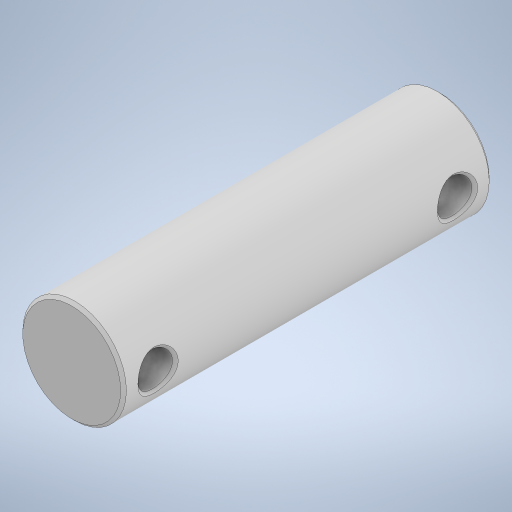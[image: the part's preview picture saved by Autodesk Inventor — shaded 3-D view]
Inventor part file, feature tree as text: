
AUTODESK INVENTOR PART (.ipt)
format: ipt  version: 2023 (Build 270158000, 158)  size: 261,632 bytes
history: native  units: mm
features: sketch x2, extrude x1, hole x1, chamfer x1
ambient origin geometry x8: Origin, YZ Plane, XZ Plane, XY Plane, X Axis, Y Axis, Z Axis, Center Point
bodies: Solido1 (feature_tree)
feature tree (5):
  extrude  "Estrusione1"  Depth=64.0mm TaperAngle=0.0deg
  hole  "Foro1"  [1 undecoded]
  chamfer  "Smusso1"  Distance=52.0mm
  sketch  "Schizzo1"
  sketch  "Schizzo2"
note: 1 required parameter value undecoded (feature->parameter linkage not recoverable at this tier; creation-order binding heuristic only, values carry confidence <= 0.55)
